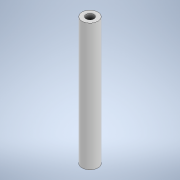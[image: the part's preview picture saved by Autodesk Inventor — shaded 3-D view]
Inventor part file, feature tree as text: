
AUTODESK INVENTOR PART (.ipt)
format: ipt  version: 2022.2 (Build 262287010, 287A)  size: 94,720 bytes
history: native  units: in
note: dims shown in document units (in); Inventor stores cm internally (conversion verified against a paired STEP export)
features: other x1, extrude x1, sketch x1
ambient origin geometry x8: Origin, YZ Plane, XZ Plane, XY Plane, X Axis, Y Axis, Z Axis, Center Point
bodies: Body1 (feature_tree)
feature tree (3):
  other  "Sólido1"
  extrude  "Extrusión1"  Depth=0.0984in
  sketch  "Boceto1"  dims[d0=0.1969in d1=0.0984in d2=1.5748in d3=0.0in]
